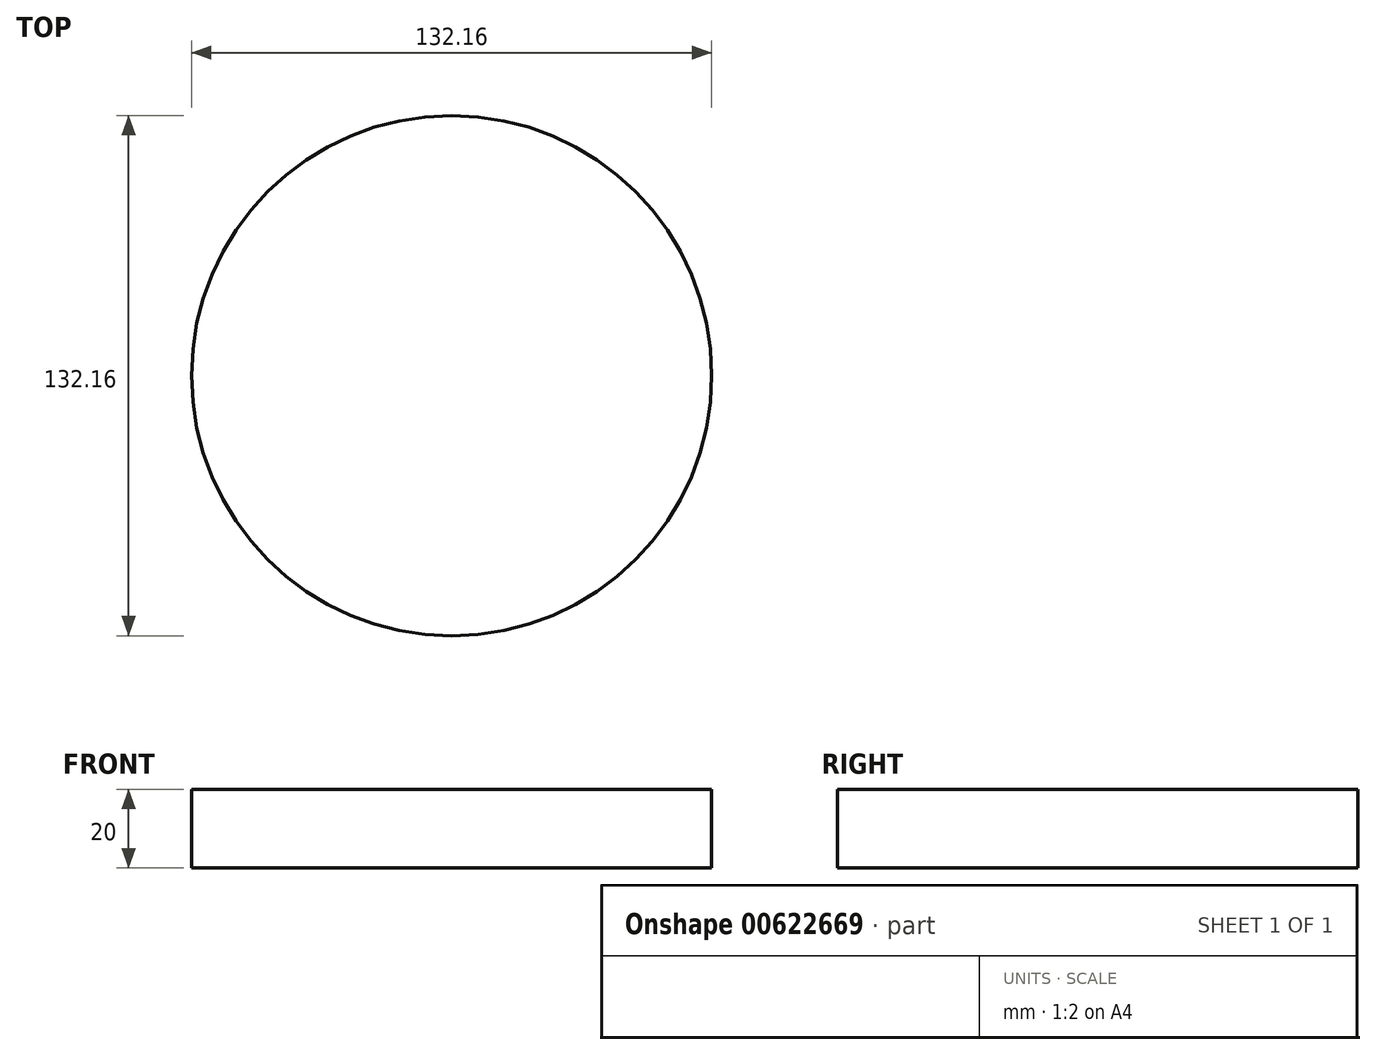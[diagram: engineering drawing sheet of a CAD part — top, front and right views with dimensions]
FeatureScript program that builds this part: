
annotation { "Feature Type Name" : "Feature", "Feature Type Description" : "" }
export const myFeature = defineFeature(function(context is Context, id is Id, definition is map)
    precondition{}
    {
        {
            var Q0;
            Q0=qCreatedBy(makeId("Top.planeOp"),FACE);
            var sketch = newSketch(context, id + "F0", { "sketchPlane" : qUnion([Q0])});
            skCircle(sketch, "E0", {"center": v(0, 0) * mm, "radius": 66.08 * mm});
            skSolve(sketch);
        }
        {
            var Q0;
            Q0 = qSketchRegion(id + "F0", true);
            extrude(context, id + "F1", {"entities" : qUnion([Q0]), "depth" : 20 * mm, "offsetDistance" : 25.4 * mm});
        }
    });
